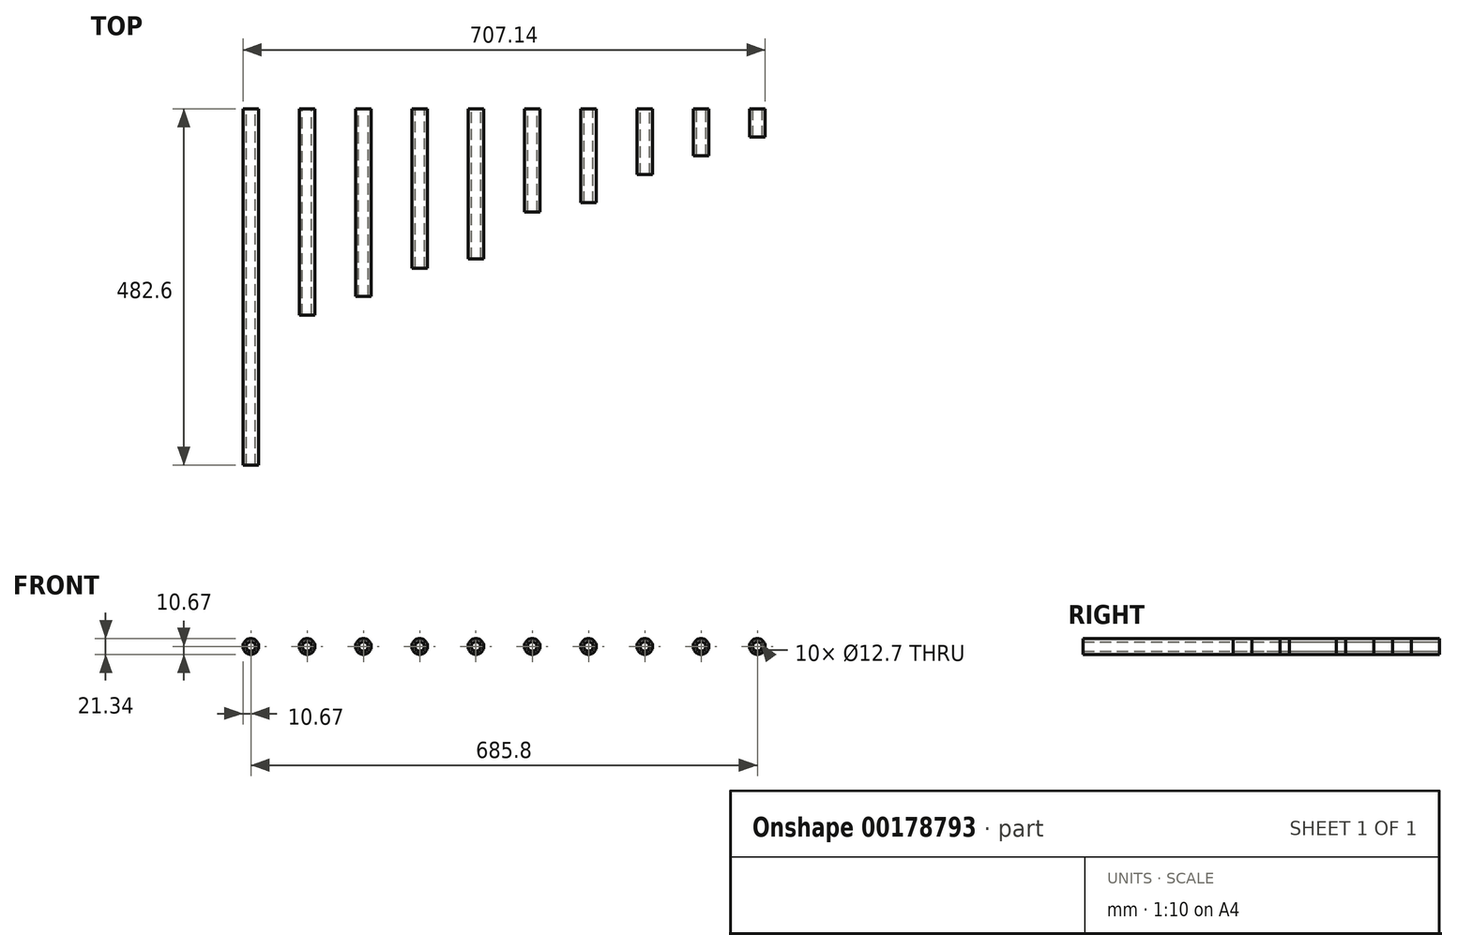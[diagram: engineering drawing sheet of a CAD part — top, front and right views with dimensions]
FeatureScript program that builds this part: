
annotation { "Feature Type Name" : "Feature", "Feature Type Description" : "" }
export const myFeature = defineFeature(function(context is Context, id is Id, definition is map)
    precondition{}
    {
        {
            var Q0;
            Q0=qCreatedBy(makeId("Front.planeOp"),FACE);
            var sketch = newSketch(context, id + "F0", { "sketchPlane" : qUnion([Q0])});
            skCircle(sketch, "E0", {"center": v(0, 0) * mm, "radius": 10.67 * mm});
            skCircle(sketch, "E1", {"center": v(0, 0) * mm, "radius": 6.35 * mm});
            skSolve(sketch);
        }
        {
            var Q0;
            Q0=makeQuery(id+"F0.imprint","IMPRINT",FACE,{"disambiguationData":[TD([[makeQuery(id+"F0.imprint","IMPRINT",EDGE,{"derivedFrom":sQuery(id+"F0.wireOp",EDGE,"E0")}),1.0]])]});
            extrude(context, id + "F1", {"entities" : qUnion([Q0]), "depth" : 482.6 * mm});
        }
        {
            var Q0;
            Q0=qCreatedBy(makeId("Front.planeOp"),FACE);
            var sketch = newSketch(context, id + "F2", { "sketchPlane" : qUnion([Q0])});
            skCircle(sketch, "E2", {"center": v(76.2, 0) * mm, "radius": 10.67 * mm});
            skCircle(sketch, "E3", {"center": v(76.2, 0) * mm, "radius": 6.35 * mm});
            skSolve(sketch);
        }
        {
            var Q0;
            Q0=makeQuery(id+"F2.imprint","IMPRINT",FACE,{"disambiguationData":[TD([[makeQuery(id+"F2.imprint","IMPRINT",EDGE,{"derivedFrom":sQuery(id+"F2.wireOp",EDGE,"E2")}),1.0]])]});
            extrude(context, id + "F3", {"entities" : qUnion([Q0]), "depth" : 279.4 * mm});
        }
        {
            var Q0;
            Q0=qCreatedBy(makeId("Front.planeOp"),FACE);
            var sketch = newSketch(context, id + "F4", { "sketchPlane" : qUnion([Q0])});
            skCircle(sketch, "E4", {"center": v(152.4, 0) * mm, "radius": 10.67 * mm});
            skCircle(sketch, "E5", {"center": v(152.4, 0) * mm, "radius": 6.35 * mm});
            skSolve(sketch);
        }
        {
            var Q0;
            Q0=makeQuery(id+"F4.imprint","IMPRINT",FACE,{"disambiguationData":[TD([[makeQuery(id+"F4.imprint","IMPRINT",EDGE,{"derivedFrom":sQuery(id+"F4.wireOp",EDGE,"E4")}),1.0]])]});
            extrude(context, id + "F5", {"entities" : qUnion([Q0]), "depth" : 254 * mm});
        }
        {
            var Q0;
            Q0=qCreatedBy(makeId("Front.planeOp"),FACE);
            var sketch = newSketch(context, id + "F6", { "sketchPlane" : qUnion([Q0])});
            skCircle(sketch, "E6", {"center": v(228.6, 0) * mm, "radius": 10.67 * mm});
            skCircle(sketch, "E7", {"center": v(228.6, 0) * mm, "radius": 6.35 * mm});
            skSolve(sketch);
        }
        {
            var Q0;
            Q0=makeQuery(id+"F6.imprint","IMPRINT",FACE,{"disambiguationData":[TD([[makeQuery(id+"F6.imprint","IMPRINT",EDGE,{"derivedFrom":sQuery(id+"F6.wireOp",EDGE,"E6")}),1.0]])]});
            extrude(context, id + "F7", {"entities" : qUnion([Q0]), "depth" : 215.9 * mm});
        }
        {
            var Q0;
            Q0=qCreatedBy(makeId("Front.planeOp"),FACE);
            var sketch = newSketch(context, id + "F8", { "sketchPlane" : qUnion([Q0])});
            skCircle(sketch, "E8", {"center": v(304.8, 0) * mm, "radius": 10.67 * mm});
            skCircle(sketch, "E9", {"center": v(304.8, 0) * mm, "radius": 6.35 * mm});
            skSolve(sketch);
        }
        {
            var Q0;
            Q0=makeQuery(id+"F8.imprint","IMPRINT",FACE,{"disambiguationData":[TD([[makeQuery(id+"F8.imprint","IMPRINT",EDGE,{"derivedFrom":sQuery(id+"F8.wireOp",EDGE,"E8")}),1.0]])]});
            extrude(context, id + "F9", {"entities" : qUnion([Q0]), "depth" : 203.2 * mm});
        }
        {
            var Q0;
            Q0=qCreatedBy(makeId("Front.planeOp"),FACE);
            var sketch = newSketch(context, id + "F10", { "sketchPlane" : qUnion([Q0])});
            skCircle(sketch, "E10", {"center": v(381, 0) * mm, "radius": 10.67 * mm});
            skCircle(sketch, "E11", {"center": v(381, 0) * mm, "radius": 6.35 * mm});
            skSolve(sketch);
        }
        {
            var Q0;
            Q0=makeQuery(id+"F10.imprint","IMPRINT",FACE,{"disambiguationData":[TD([[makeQuery(id+"F10.imprint","IMPRINT",EDGE,{"derivedFrom":sQuery(id+"F10.wireOp",EDGE,"E10")}),1.0]])]});
            extrude(context, id + "F11", {"entities" : qUnion([Q0]), "depth" : 139.7 * mm});
        }
        {
            var Q0;
            Q0=qCreatedBy(makeId("Front.planeOp"),FACE);
            var sketch = newSketch(context, id + "F12", { "sketchPlane" : qUnion([Q0])});
            skCircle(sketch, "E12", {"center": v(457.2, 0) * mm, "radius": 10.67 * mm});
            skCircle(sketch, "E13", {"center": v(457.2, 0) * mm, "radius": 6.35 * mm});
            skSolve(sketch);
        }
        {
            var Q0;
            Q0=makeQuery(id+"F12.imprint","IMPRINT",FACE,{"disambiguationData":[TD([[makeQuery(id+"F12.imprint","IMPRINT",EDGE,{"derivedFrom":sQuery(id+"F12.wireOp",EDGE,"E12")}),1.0]])]});
            extrude(context, id + "F13", {"entities" : qUnion([Q0]), "depth" : 127 * mm});
        }
        {
            var Q0;
            Q0=qCreatedBy(makeId("Front.planeOp"),FACE);
            var sketch = newSketch(context, id + "F14", { "sketchPlane" : qUnion([Q0])});
            skCircle(sketch, "E14", {"center": v(533.4, 0) * mm, "radius": 10.67 * mm});
            skCircle(sketch, "E15", {"center": v(533.4, 0) * mm, "radius": 6.35 * mm});
            skSolve(sketch);
        }
        {
            var Q0;
            Q0=makeQuery(id+"F14.imprint","IMPRINT",FACE,{"disambiguationData":[TD([[makeQuery(id+"F14.imprint","IMPRINT",EDGE,{"derivedFrom":sQuery(id+"F14.wireOp",EDGE,"E14")}),1.0]])]});
            extrude(context, id + "F15", {"entities" : qUnion([Q0]), "depth" : 88.9 * mm});
        }
        {
            var Q0;
            Q0=qCreatedBy(makeId("Front.planeOp"),FACE);
            var sketch = newSketch(context, id + "F16", { "sketchPlane" : qUnion([Q0])});
            skCircle(sketch, "E16", {"center": v(609.6, 0) * mm, "radius": 10.67 * mm});
            skCircle(sketch, "E17", {"center": v(609.6, 0) * mm, "radius": 6.35 * mm});
            skSolve(sketch);
        }
        {
            var Q0;
            Q0=makeQuery(id+"F16.imprint","IMPRINT",FACE,{"disambiguationData":[TD([[makeQuery(id+"F16.imprint","IMPRINT",EDGE,{"derivedFrom":sQuery(id+"F16.wireOp",EDGE,"E16")}),1.0]])]});
            extrude(context, id + "F17", {"entities" : qUnion([Q0]), "depth" : 63.5 * mm});
        }
        {
            var Q0;
            Q0=qCreatedBy(makeId("Front.planeOp"),FACE);
            var sketch = newSketch(context, id + "F18", { "sketchPlane" : qUnion([Q0])});
            skCircle(sketch, "E18", {"center": v(685.8, 0) * mm, "radius": 10.67 * mm});
            skCircle(sketch, "E19", {"center": v(685.8, 0) * mm, "radius": 6.35 * mm});
            skSolve(sketch);
        }
        {
            var Q0;
            Q0=makeQuery(id+"F18.imprint","IMPRINT",FACE,{"disambiguationData":[TD([[makeQuery(id+"F18.imprint","IMPRINT",EDGE,{"derivedFrom":sQuery(id+"F18.wireOp",EDGE,"E18")}),1.0]])]});
            extrude(context, id + "F19", {"entities" : qUnion([Q0]), "depth" : 38.1 * mm});
        }
    });
